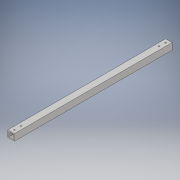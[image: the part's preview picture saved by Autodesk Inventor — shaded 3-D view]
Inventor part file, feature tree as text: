
AUTODESK INVENTOR PART (.ipt)
format: ipt  version: 2018 (Build 220112000, 112)  size: 117,248 bytes
history: native  units: in
note: dims shown in document units (in); Inventor stores cm internally (conversion verified against a paired STEP export)
features: extrude x2, sketch x2
ambient origin geometry x8: Origin, YZ Plane, XZ Plane, XY Plane, X Axis, Y Axis, Z Axis, Center Point
bodies: Solid1 (feature_tree)
feature tree (4):
  extrude  "Extrusion1"  Depth=1.0in
  extrude  "Extrusion2"  Depth=24.0in TaperAngle=0.0deg
  sketch  "Sketch1"  dims[d0=1.0in d1=1.0in]
  sketch  "Sketch2"  dims[d2=0.125in d3=24.0in d4=0.0in d5=0.5in d6=1.0in d7=0.2031in d8=24.0in d9=0.0in]
